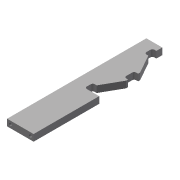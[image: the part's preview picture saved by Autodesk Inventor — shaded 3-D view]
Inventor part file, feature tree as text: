
AUTODESK INVENTOR PART (.ipt)
format: ipt  version: 2016 (Build 200138000, 138)  size: 145,920 bytes
history: native  units: mm
features: extrude x3, hole x1
ambient origin geometry x8: Origin, YZ Plane, XZ Plane, XY Plane, X Axis, Y Axis, Z Axis, Center Point
bodies: Volumenkörper1 (feature_tree)
feature tree (4):
  extrude  "Extrusion1"  Depth=210.0mm
  extrude  "Extrusion2"  Depth=40.0mm
  extrude  "Extrusion3"  Depth=10.0mm TaperAngle=0.0deg
  hole  "Bohrung1"  [1 undecoded]
note: 1 required parameter value undecoded (feature->parameter linkage not recoverable at this tier; creation-order binding heuristic only, values carry confidence <= 0.55)
